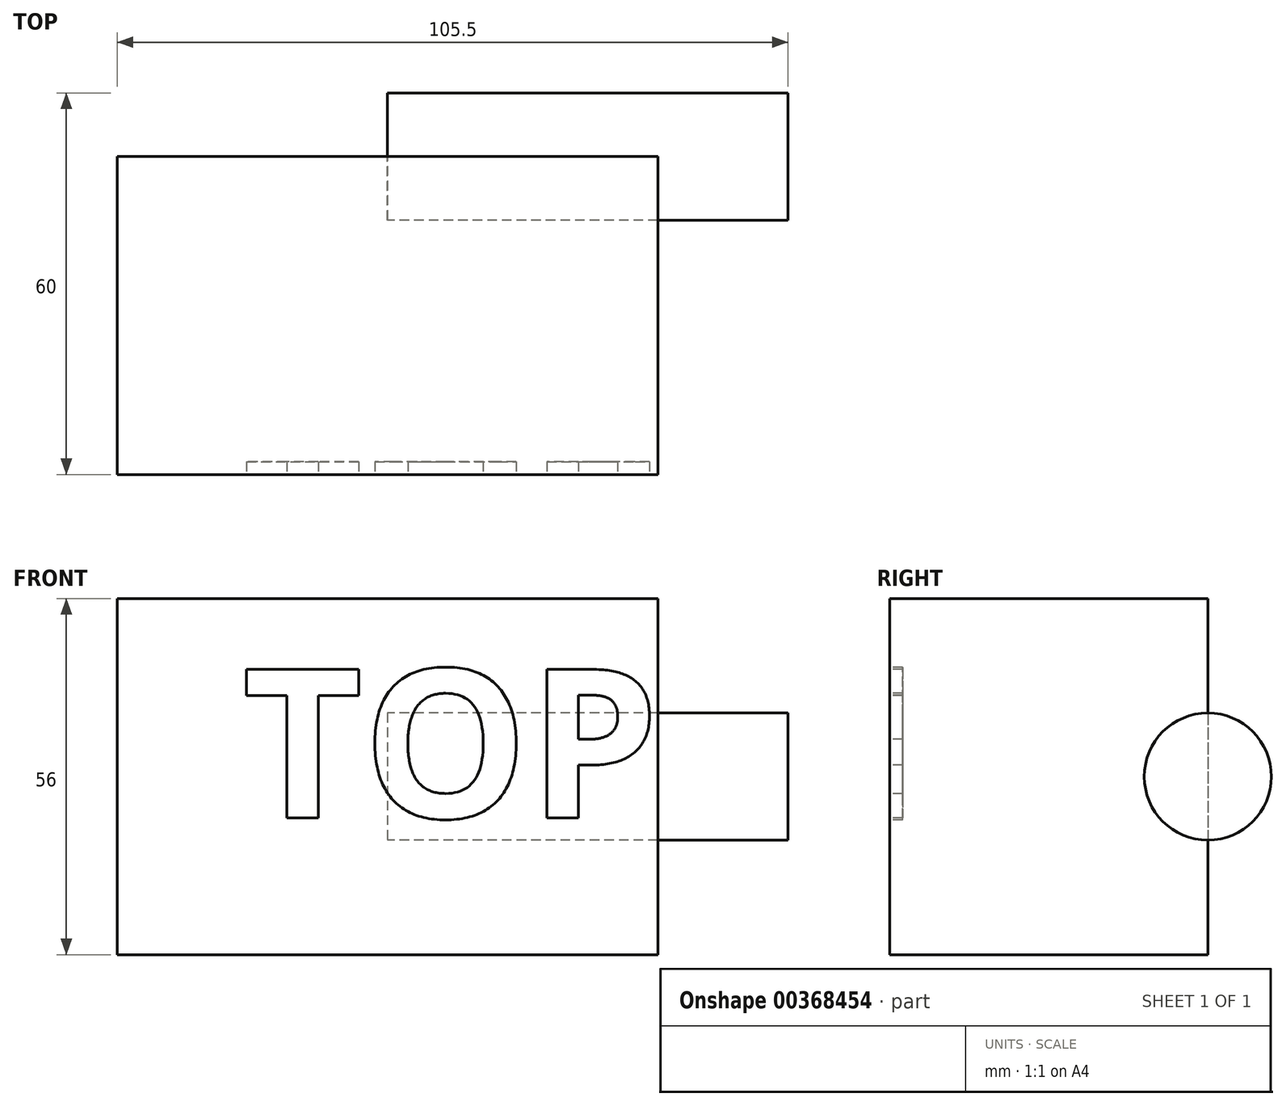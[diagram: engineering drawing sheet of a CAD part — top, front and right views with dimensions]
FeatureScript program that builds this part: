
annotation { "Feature Type Name" : "Feature", "Feature Type Description" : "" }
export const myFeature = defineFeature(function(context is Context, id is Id, definition is map)
    precondition{}
    {
        {
            var Q0;
            Q0=qCreatedBy(makeId("Front.planeOp"),FACE);
            var sketch = newSketch(context, id + "F0", { "sketchPlane" : qUnion([Q0])});
            skLineSegment(sketch, "E0.bottom", {"start": v(0, 0) * mm, "end": v(63, 0) * mm});
            skLineSegment(sketch, "E0.top", {"start": v(0, 10) * mm, "end": v(63, 10) * mm});
            skLineSegment(sketch, "E0.left", {"start": v(0, 0) * mm, "end": v(0, 10) * mm});
            skLineSegment(sketch, "E0.right", {"start": v(63, 0) * mm, "end": v(63, 10) * mm});
            skSolve(sketch);
        }
        {
            var Q0;
            Q0 = qSketchRegion(id + "F0", true);
            var Q1;
            Q1=sQuery(id+"F0.wireOp",EDGE,"E0.bottom");
            revolve(context, id + "F1", {"entities" : qUnion([Q0]), "axis" : qUnion([Q1]), "revolveType" : RevolveType.FULL});
        }
        {
            var Q0;
            Q0=qCreatedBy(makeId("Front.planeOp"),FACE);
            var sketch = newSketch(context, id + "F2", { "sketchPlane" : qUnion([Q0])});
            skLineSegment(sketch, "E1.bottom", {"start": v(-42.5, 28) * mm, "end": v(42.5, 28) * mm});
            skLineSegment(sketch, "E1.top", {"start": v(-42.5, -28) * mm, "end": v(42.5, -28) * mm});
            skLineSegment(sketch, "E1.left", {"start": v(-42.5, 28) * mm, "end": v(-42.5, -28) * mm});
            skLineSegment(sketch, "E1.right", {"start": v(42.5, 28) * mm, "end": v(42.5, -28) * mm});
            skSolve(sketch);
        }
        {
            var Q0;
            Q0=makeQuery(id+"F2.imprint","IMPRINT",FACE,{"disambiguationData":[TD([[makeQuery(id+"F2.imprint","IMPRINT",EDGE,{"derivedFrom":sQuery(id+"F2.wireOp",EDGE,"E1.bottom")}),-1.0]])]});
            extrude(context, id + "F3", {"entities" : qUnion([Q0]), "depth" : 50 * mm});
        }
        {
            var Q0;
            Q0=makeQuery(id+"F3.opExtrude","CAP_FACE",FACE,{"disambiguationData":[OSD([sQuery(id+"F2.wireOp",EDGE,"E1.bottom"),sQuery(id+"F2.wireOp",EDGE,"E1.top"),sQuery(id+"F2.wireOp",EDGE,"E1.left"),sQuery(id+"F2.wireOp",EDGE,"E1.right")])],"isStart":false});
            var sketch = newSketch(context, id + "F4", { "sketchPlane" : qUnion([Q0])});
            skText(sketch, "E2", { "text": "TOP", "fontName": "OpenSans-Bold.ttf"});
            const initialGuessF4  = {"E2": [-0.02282, -0.00649, 1, 0, 0.02354]};
            skSetInitialGuess(sketch, initialGuessF4);
            skSolve(sketch);
        }
        {
            var Q0;
            Q0=makeQuery(id+"F4.imprint","IMPRINT",FACE,{"disambiguationData":[TD([[makeQuery(id+"F4.imprint","IMPRINT",EDGE,{"derivedFrom":sQuery(id+"F4.wireOp",EDGE,"E2.sketch_text.stroke-0")}),-1.0]])]});
            var Q1;
            Q1 = qSketchRegion(id + "F4", true);
            extrude(context, id + "F5", {"entities" : qUnion([Q0, Q1]), "operationType" : NewBodyOperationType.REMOVE, "oppositeDirection" : true, "depth" : 2 * mm});
        }
    });
